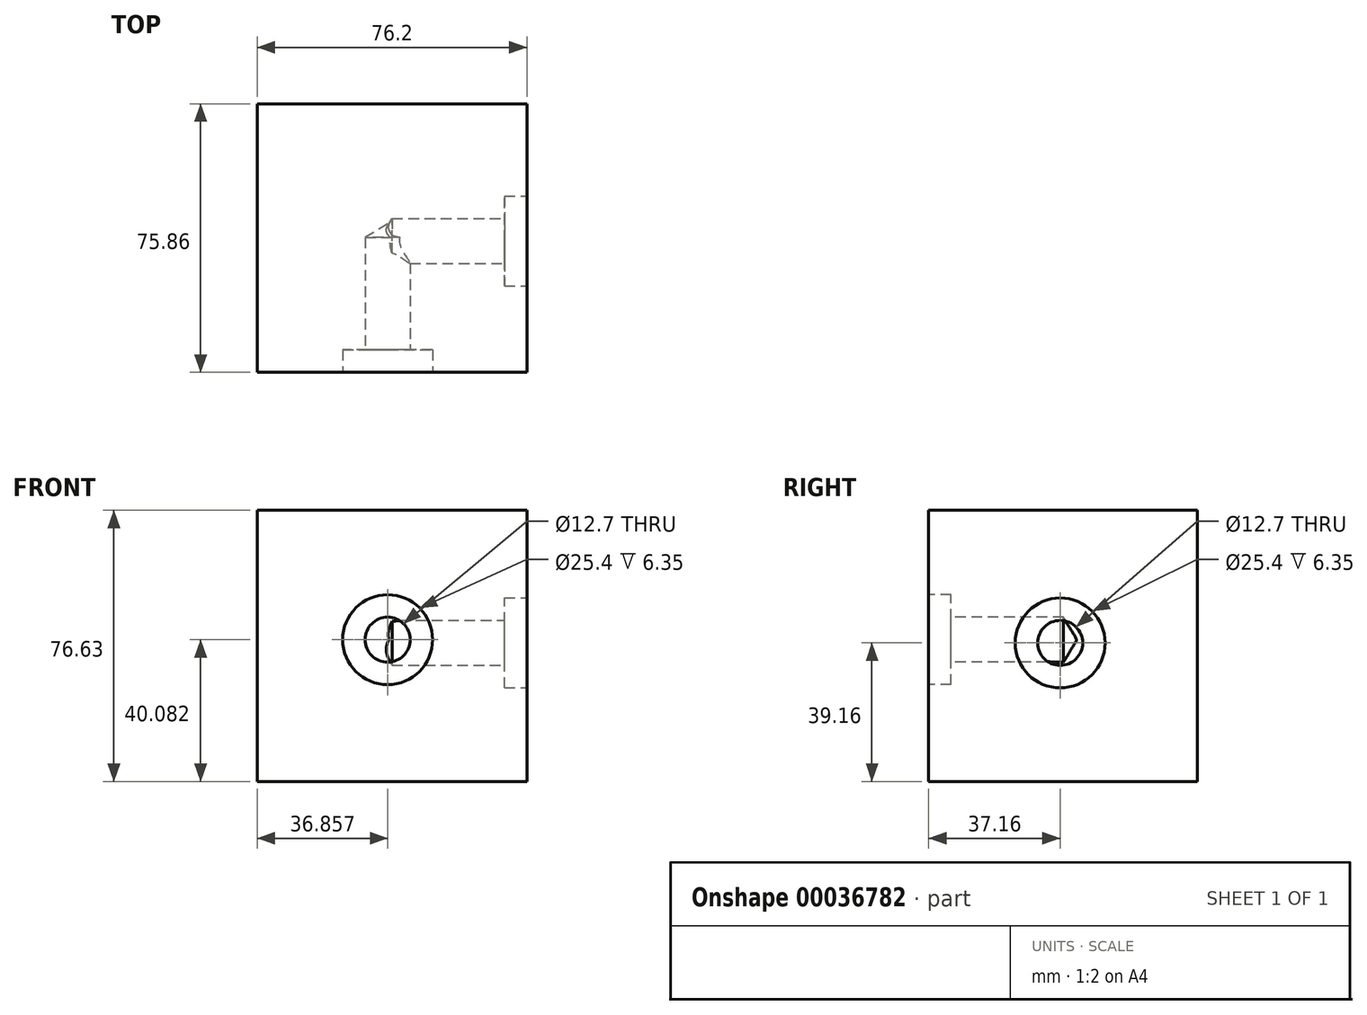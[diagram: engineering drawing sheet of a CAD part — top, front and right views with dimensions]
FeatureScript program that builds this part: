
annotation { "Feature Type Name" : "Feature", "Feature Type Description" : "" }
export const myFeature = defineFeature(function(context is Context, id is Id, definition is map)
    precondition{}
    {
        {
            var Q0;
            Q0=qCreatedBy(makeId("Right.planeOp"),FACE);
            var sketch = newSketch(context, id + "F0", { "sketchPlane" : qUnion([Q0])});
            skLineSegment(sketch, "E0.bottom", {"start": v(0, 0) * mm, "end": v(-75.86, 0) * mm});
            skLineSegment(sketch, "E0.top", {"start": v(0, 76.63) * mm, "end": v(-75.86, 76.63) * mm});
            skLineSegment(sketch, "E0.left", {"start": v(0, 0) * mm, "end": v(0, 76.63) * mm});
            skLineSegment(sketch, "E0.right", {"start": v(-75.86, 0) * mm, "end": v(-75.86, 76.63) * mm});
            skSolve(sketch);
        }
        {
            var Q0;
            Q0=makeQuery(id+"F0.imprint","IMPRINT",FACE,{"disambiguationData":[TD([[makeQuery(id+"F0.imprint","IMPRINT",EDGE,{"derivedFrom":sQuery(id+"F0.wireOp",EDGE,"E0.bottom")}),-1.0]])]});
            extrude(context, id + "F1", {"entities" : qUnion([Q0]), "depth" : 76.2 * mm});
        }
        {
            var Q0;
            Q0=makeQuery(id+"F1.opExtrude","SWEPT_FACE",FACE,{"disambiguationData":[OSD([sQuery(id+"F0.wireOp",EDGE,"E0.right")])]});
            var sketch = newSketch(context, id + "F2", { "sketchPlane" : qUnion([Q0])});
            skPoint(sketch, "E1", {"position": v(36.86, 40.08) * mm});
            skSolve(sketch);
        }
        {
            var Q0;
            Q0=sQuery(id+"F2.wireOp",VERTEX,"E1");
            var Q1;
            Q1=makeQuery(id+"F1.opExtrude","SWEPT_BODY",BODY,{"disambiguationData":[OSD([sQuery(id+"F0.wireOp",EDGE,"E0.bottom"),sQuery(id+"F0.wireOp",EDGE,"E0.top"),sQuery(id+"F0.wireOp",EDGE,"E0.left"),sQuery(id+"F0.wireOp",EDGE,"E0.right")])]});
            hole(context, id + "F3", {"style" : HoleStyle.C_BORE, "holeDiameter" : 12.7 * mm, "cBoreDiameter" : 25.4 * mm, "cBoreDepth" : 6.35 * mm, "endStyle" : HoleEndStyle.BLIND, "holeDepth" : 38.1 * mm, "locations" : qUnion([Q0]), "scope" : qUnion([Q1])});
        }
        {
            var Q0;
            Q0=makeQuery(id+"F1.opExtrude","CAP_FACE",FACE,{"disambiguationData":[OSD([sQuery(id+"F0.wireOp",EDGE,"E0.bottom"),sQuery(id+"F0.wireOp",EDGE,"E0.top"),sQuery(id+"F0.wireOp",EDGE,"E0.left"),sQuery(id+"F0.wireOp",EDGE,"E0.right")])],"isStart":false});
            var sketch = newSketch(context, id + "F4", { "sketchPlane" : qUnion([Q0])});
            skPoint(sketch, "E2", {"position": v(-38.7, 39.16) * mm});
            skSolve(sketch);
        }
        {
            var Q0;
            Q0=sQuery(id+"F4.wireOp",VERTEX,"E2");
            var Q1;
            Q1=makeQuery(id+"F1.opExtrude","SWEPT_BODY",BODY,{"disambiguationData":[OSD([sQuery(id+"F0.wireOp",EDGE,"E0.bottom"),sQuery(id+"F0.wireOp",EDGE,"E0.top"),sQuery(id+"F0.wireOp",EDGE,"E0.left"),sQuery(id+"F0.wireOp",EDGE,"E0.right")])]});
            hole(context, id + "F5", {"style" : HoleStyle.C_BORE, "holeDiameter" : 12.7 * mm, "cBoreDiameter" : 25.4 * mm, "cBoreDepth" : 6.35 * mm, "endStyle" : HoleEndStyle.BLIND, "holeDepth" : 38.1 * mm, "locations" : qUnion([Q0]), "scope" : qUnion([Q1])});
        }
    });
